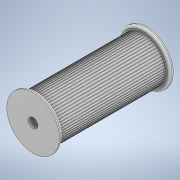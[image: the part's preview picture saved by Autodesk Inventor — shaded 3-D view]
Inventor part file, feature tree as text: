
AUTODESK INVENTOR PART (.ipt)
format: ipt  version: 2020 (Build 240168000, 168)  size: 322,048 bytes
history: mixed  units: in
note: dims shown in document units (in); Inventor stores cm internally (conversion verified against a paired STEP export)
features: sketch x1, fillet x1, imported_body x1
ambient origin geometry x8: Origin, YZ Plane, XZ Plane, XY Plane, X Axis, Y Axis, Z Axis, Center Point
bodies: Solid1 (imported_parasolid)
feature tree (3):
  sketch  "Sketch4"
  fillet  "Fillet1"  [1 undecoded]
  imported_body  NMx_Import_Brep_tag  [imported B-rep: ~129 faces, bbox_mm=[44.4, 37.662953, 96.0]]
note: 1 required parameter value undecoded (feature->parameter linkage not recoverable at this tier; creation-order binding heuristic only, values carry confidence <= 0.55)
